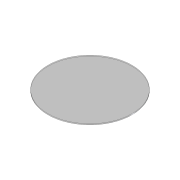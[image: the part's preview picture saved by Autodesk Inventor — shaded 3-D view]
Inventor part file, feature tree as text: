
AUTODESK INVENTOR PART (.ipt)
format: ipt  version: 2022 (Build 260153000, 153)  size: 75,776 bytes
history: native  units: mm
features: extrude x1, sketch x1
ambient origin geometry x8: Origin, YZ Plane, XZ Plane, XY Plane, X Axis, Y Axis, Z Axis, Center Point
bodies: Volumenkörper1 (feature_tree)
feature tree (2):
  extrude  "Extrusion1"  Depth=0.125mm TaperAngle=0.0deg
  sketch  "Skizze1"  dims[d0=10.0mm d1=0.125mm d2=0.0mm]
